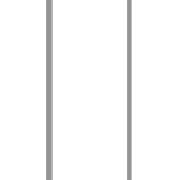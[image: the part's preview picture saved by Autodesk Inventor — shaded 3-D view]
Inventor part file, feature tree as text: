
AUTODESK INVENTOR PART (.ipt)
format: ipt  version: 2021 (Build 250183000, 183)  size: 150,528 bytes
history: native  units: in
note: dims shown in document units (in); Inventor stores cm internally (conversion verified against a paired STEP export)
features: plane x5, sketch x5, other x4, hole x1, extrude x1, boolean_combine x1
ambient origin geometry x8: Origin, YZ Plane, XZ Plane, XY Plane, X Axis, Y Axis, Z Axis, Center Point
bodies: Solid1 (feature_tree), Body (feature_tree), Solid2 (feature_tree)
feature tree (17):
  other  "Driven Length"
  other  "Frame Generator"
  plane  "Work Plane3"
  other  "Start Plane"
  other  "End Plane"
  hole  "Hole2"  [1 undecoded]
  plane  "Work Plane7"
  plane  "Work Plane8"
  plane  "Work Plane9"
  extrude  "Extrusion3"  Depth=0.0625in
  boolean_combine  "Combine1"
  sketch  "Sketch"  dims[d17=2.0in d18=0.12in d19=0.0in d22=1.5in d23=0.4375in d24=0.75in d25=0.635in d26=0.25in d27=0.5635in d28=1.0in d29=0.8108in d32=90.0deg d21=2.0in d34=0.12in d35=0.0in d8=0.5in d9=0.0344in d10=0.5in d11=0.0344in]
  sketch  "Sketch5"  dims[d0=1.5in d1=1.0in]
  sketch  "Sketch8"  dims[d2=0.0625in d3=0.0625in]
  plane  "Work Plane6"
  sketch  "Sketch9"  dims[d4=2.0in]
  sketch  "Sketch10"  dims[d16=-0.0in]
note: 1 required parameter value undecoded (feature->parameter linkage not recoverable at this tier; creation-order binding heuristic only, values carry confidence <= 0.55)
